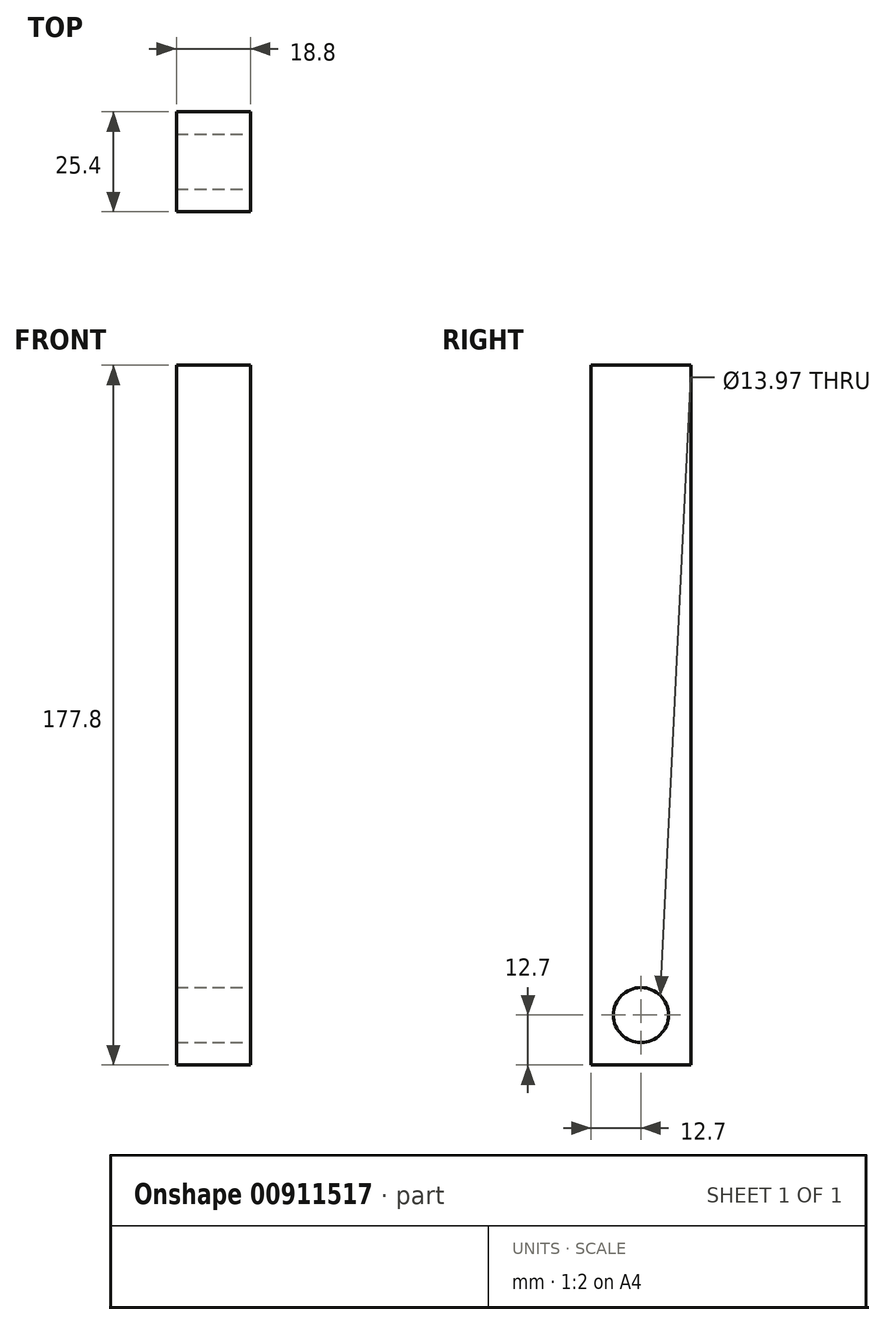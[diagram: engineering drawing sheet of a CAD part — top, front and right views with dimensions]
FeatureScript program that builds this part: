
annotation { "Feature Type Name" : "Feature", "Feature Type Description" : "" }
export const myFeature = defineFeature(function(context is Context, id is Id, definition is map)
    precondition{}
    {
        {
            var Q0;
            Q0=qCreatedBy(makeId("Top.planeOp"),FACE);
            var sketch = newSketch(context, id + "F0", { "sketchPlane" : qUnion([Q0])});
            skLineSegment(sketch, "E0.bottom", {"start": v(0, 0) * mm, "end": v(-18.8, 0) * mm});
            skLineSegment(sketch, "E0.top", {"start": v(0, 25.4) * mm, "end": v(-18.8, 25.4) * mm});
            skLineSegment(sketch, "E0.left", {"start": v(0, 0) * mm, "end": v(0, 25.4) * mm});
            skLineSegment(sketch, "E0.right", {"start": v(-18.8, 0) * mm, "end": v(-18.8, 25.4) * mm});
            skSolve(sketch);
        }
        {
            var Q0;
            Q0=makeQuery(id+"F0.imprint","IMPRINT",FACE,{"disambiguationData":[TD([[makeQuery(id+"F0.imprint","IMPRINT",EDGE,{"derivedFrom":sQuery(id+"F0.wireOp",EDGE,"E0.bottom")}),-1.0]])]});
            extrude(context, id + "F1", {"entities" : qUnion([Q0]), "depth" : 177.8 * mm, "offsetDistance" : 25.4 * mm});
        }
        {
            var Q0;
            Q0=makeQuery(id+"F1.opExtrude","SWEPT_FACE",FACE,{"disambiguationData":[OSD([sQuery(id+"F0.wireOp",EDGE,"E0.left")])]});
            var sketch = newSketch(context, id + "F2", { "sketchPlane" : qUnion([Q0])});
            skCircle(sketch, "E1", {"center": v(12.7, 12.7) * mm, "radius": 6.99 * mm});
            skSolve(sketch);
        }
        {
            var Q0;
            Q0=makeQuery(id+"F2.imprint","IMPRINT",FACE,{"disambiguationData":[TD([[makeQuery(id+"F2.imprint","IMPRINT",EDGE,{"derivedFrom":sQuery(id+"F2.wireOp",EDGE,"E1")}),1.0]])]});
            extrude(context, id + "F3", {"entities" : qUnion([Q0]), "operationType" : NewBodyOperationType.REMOVE, "oppositeDirection" : true, "depth" : 25.4 * mm, "offsetDistance" : 25.4 * mm});
        }
    });
